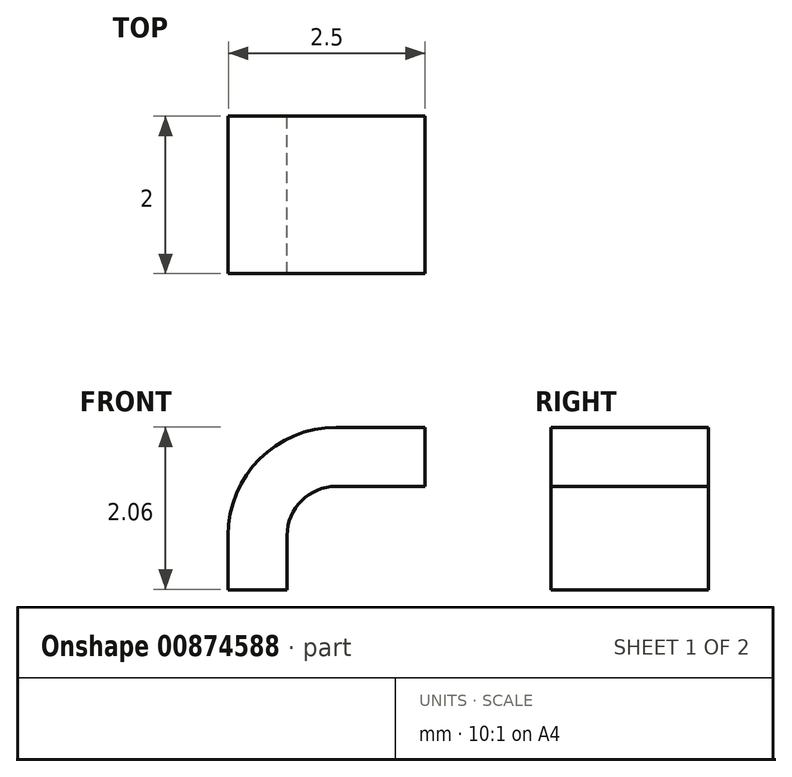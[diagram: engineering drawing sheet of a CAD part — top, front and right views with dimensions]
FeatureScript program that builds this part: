
annotation { "Feature Type Name" : "Feature", "Feature Type Description" : "" }
export const myFeature = defineFeature(function(context is Context, id is Id, definition is map)
    precondition{}
    {
        {
            var Q0;
            Q0=qCreatedBy(makeId("Front.planeOp"),FACE);
            var sketch = newSketch(context, id + "F0", { "sketchPlane" : qUnion([Q0])});
            skLineSegment(sketch, "E0.bottom", {"start": v(1.63, -0.37) * mm, "end": v(-1.62, -0.38) * mm});
            skLineSegment(sketch, "E0.top", {"start": v(1.62, 0.38) * mm, "end": v(-1.63, 0.38) * mm});
            skLineSegment(sketch, "E0.left", {"start": v(1.63, -0.37) * mm, "end": v(1.62, 0.38) * mm});
            skLineSegment(sketch, "E0.right", {"start": v(-1.63, -0.38) * mm, "end": v(-1.63, 0.37) * mm});
            skPoint(sketch, "E0.middle", {"position": v(0, 0) * mm});
            skLineSegment(sketch, "E1", {"start": v(1.62, 0.38) * mm, "end": v(1.62, 1.06) * mm});
            skLineSegment(sketch, "E2.bottom", {"start": v(4.37, 1.5) * mm, "end": v(2.38, 1.5) * mm});
            skLineSegment(sketch, "E2.top", {"start": v(4.38, 2.63) * mm, "end": v(2.38, 2.63) * mm});
            skLineSegment(sketch, "E2.left", {"start": v(4.38, 1.5) * mm, "end": v(4.38, 2.63) * mm});
            skLineSegment(sketch, "E2.right", {"start": v(2.38, 1.5) * mm, "end": v(2.38, 2.63) * mm});
            skPoint(sketch, "E2.middle", {"position": v(3.38, 2.06) * mm});
            skArc(sketch, "E3", {"start": v(1.62, 1.06) * mm, "mid": v(1.8, 1.5) * mm, "end": v(2.25, 1.69) * mm});
            skLineSegment(sketch, "E4", {"start": v(2.25, 1.69) * mm, "end": v(3.38, 1.69) * mm});
            skLineSegment(sketch, "E5.0", {"start": v(2.25, 2.44) * mm, "end": v(3.38, 2.44) * mm});
            skArc(sketch, "E5.1", {"start": v(0.87, 1.06) * mm, "mid": v(1.28, 2.04) * mm, "end": v(2.25, 2.44) * mm});
            skLineSegment(sketch, "E5.2", {"start": v(0.87, 0.38) * mm, "end": v(0.87, 1.06) * mm});
            skLineSegment(sketch, "E6", {"start": v(3.38, 2.63) * mm, "end": v(3.38, 1.5) * mm});
            skFitSpline(sketch, "E7", {"points": [v(-1.63, 0.37) * mm, v(2.25, 2.44) * mm], "startDerivative": vector(0.04, 2.13) * mm, "endDerivative": vector(4.13, -0.11) * mm});
            skSolve(sketch);
        }
        {
            var Q0;
            {var subQ6=sQuery(id+"F0.wireOp",EDGE,"E1");Q0=makeQuery(id+"F0.imprint","IMPRINT",FACE,{"disambiguationData":[TD([[makeQuery(id+"F0.imprint","IMPRINT",EDGE,{"derivedFrom":subQ6}),1.0]])]});}
            var Q1;
            {var subQ0=sQuery(id+"F0.wireOp",EDGE,"E4");var subQ1=sQuery(id+"F0.wireOp",EDGE,"E2.right");var subQ2=makeQuery(id+"F0.imprint","INTERSECT",VERTEX,{"derivedFrom":[subQ1,subQ0]});Q1=makeQuery(id+"F0.imprint","IMPRINT",FACE,{"disambiguationData":[TD([[makeQuery(id+"F0.imprint","IMPRINT",EDGE,{"disambiguationData":[TD([[subQ2,-1.0]])],"derivedFrom":subQ1}),-1.0]])]});}
            extrude(context, id + "F1", {"entities" : qUnion([Q0, Q1]), "endBound" : BoundingType.SYMMETRIC, "depth" : 2 * mm, "offsetDistance" : 25 * mm});
        }
    });
